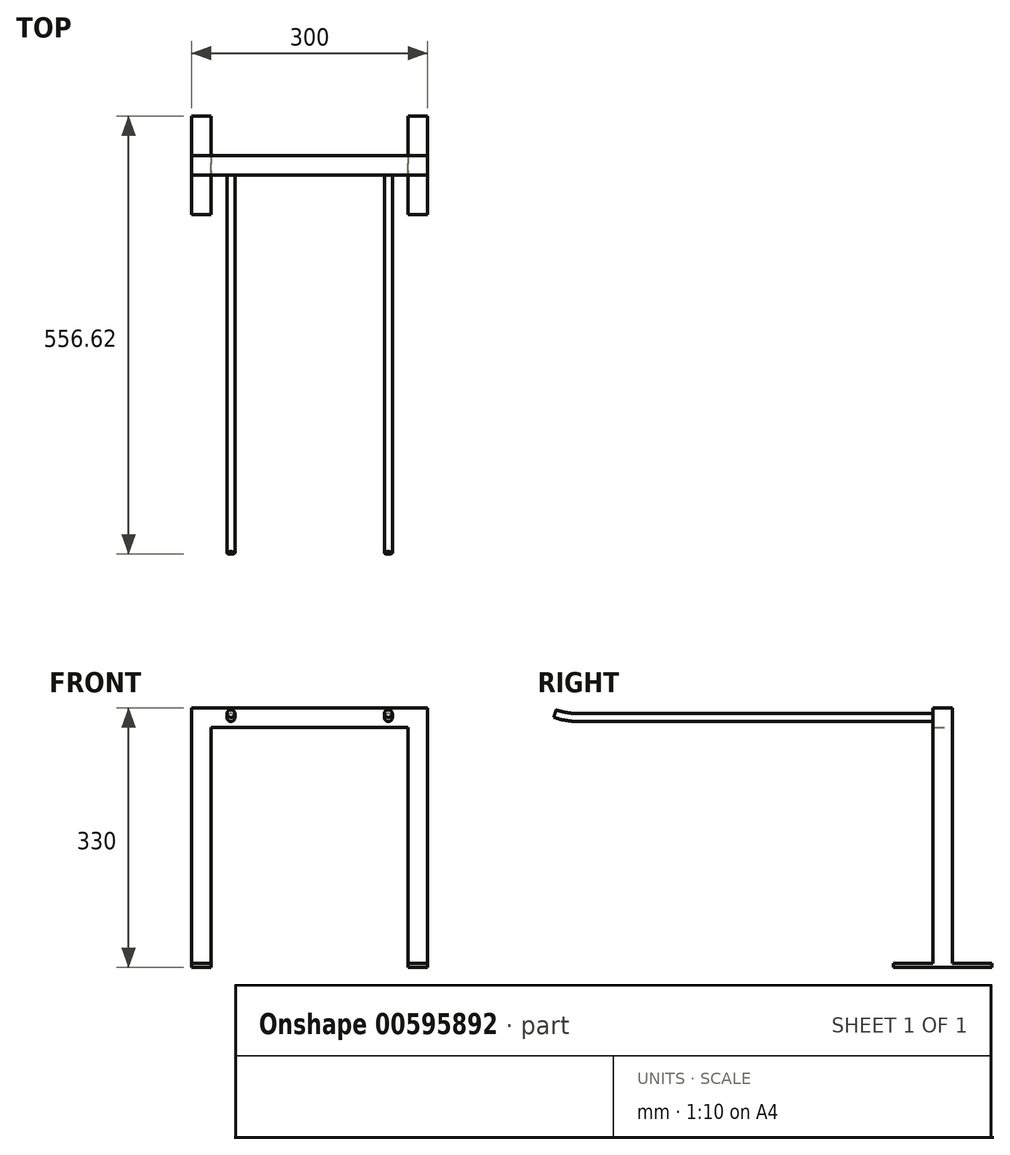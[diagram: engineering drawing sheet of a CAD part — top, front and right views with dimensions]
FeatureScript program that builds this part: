
annotation { "Feature Type Name" : "Feature", "Feature Type Description" : "" }
export const myFeature = defineFeature(function(context is Context, id is Id, definition is map)
    precondition{}
    {
        {
            var Q0;
            Q0=qCreatedBy(makeId("Right.planeOp"),FACE);
            var sketch = newSketch(context, id + "F0", { "sketchPlane" : qUnion([Q0])});
            skLineSegment(sketch, "E0.bottom", {"start": v(12.5, 12.5) * mm, "end": v(-12.5, 12.5) * mm});
            skLineSegment(sketch, "E0.top", {"start": v(12.5, -12.5) * mm, "end": v(-12.5, -12.5) * mm});
            skLineSegment(sketch, "E0.left", {"start": v(12.5, 12.5) * mm, "end": v(12.5, -12.5) * mm});
            skLineSegment(sketch, "E0.right", {"start": v(-12.5, 12.5) * mm, "end": v(-12.5, -12.5) * mm});
            skPoint(sketch, "E0.middle", {"position": v(0, 0) * mm});
            skSolve(sketch);
        }
        {
            var Q0;
            Q0=makeQuery(id+"F0.imprint","IMPRINT",FACE,{"disambiguationData":[TD([[makeQuery(id+"F0.imprint","IMPRINT",EDGE,{"derivedFrom":sQuery(id+"F0.wireOp",EDGE,"E0.bottom")}),1.0]])]});
            extrude(context, id + "F1", {"entities" : qUnion([Q0]), "depth" : 150 * mm, "offsetDistance" : 25.4 * mm, "hasSecondDirection" : true, "secondDirectionOppositeDirection" : true, "secondDirectionDepth" : 150 * mm});
        }
        {
            var Q0;
            Q0=makeQuery(id+"F1.opExtrude","SWEPT_FACE",FACE,{"disambiguationData":[OSD([sQuery(id+"F0.wireOp",EDGE,"E0.right")])]});
            var sketch = newSketch(context, id + "F2", { "sketchPlane" : qUnion([Q0])});
            skLineSegment(sketch, "E1", {"start": v(-150, 0) * mm, "end": v(150, 0) * mm, "construction": true});
            skCircle(sketch, "E2", {"center": v(-100, 0) * mm, "radius": 5 * mm});
            skCircle(sketch, "E3", {"center": v(100, 0) * mm, "radius": 5 * mm});
            skSolve(sketch);
        }
        {
            var Q0;
            Q0=qCreatedBy(makeId("Right.planeOp"),FACE);
            var sketch = newSketch(context, id + "F3", { "sketchPlane" : qUnion([Q0])});
            skLineSegment(sketch, "E4.0", {"start": v(-12.5, -5) * mm, "end": v(-12.5, 5) * mm, "construction": true});
            skLineSegment(sketch, "E5", {"start": v(-12.5, 0) * mm, "end": v(-462.5, 0) * mm});
            skArc(sketch, "E6", {"start": v(-462.5, 0) * mm, "mid": v(-477.7, 1.26) * mm, "end": v(-492.5, 5) * mm});
            skSolve(sketch);
        }
        {
            var Q0;
            Q0 = qSketchRegion(id + "F2", true);
            var Q1;
            Q1 = qConstructionFilter(qBodyType(qCreatedBy(id + "F3" ,EDGE), BodyType.WIRE), ConstructionObject.NO);
            sweep(context, id + "F4", {"operationType" : NewBodyOperationType.ADD, "profiles" : qUnion([Q0]), "path" : qUnion([Q1])});
        }
        {
            var Q0;
            Q0=makeQuery(id+"F1.opExtrude","SWEPT_FACE",FACE,{"disambiguationData":[OSD([sQuery(id+"F0.wireOp",EDGE,"E0.top")])]});
            var sketch = newSketch(context, id + "F5", { "sketchPlane" : qUnion([Q0])});
            skLineSegment(sketch, "E7.bottom", {"start": v(-150, 12.5) * mm, "end": v(-125, 12.5) * mm});
            skLineSegment(sketch, "E7.top", {"start": v(-150, -12.5) * mm, "end": v(-125, -12.5) * mm});
            skLineSegment(sketch, "E7.left", {"start": v(-150, 12.5) * mm, "end": v(-150, -12.5) * mm});
            skLineSegment(sketch, "E7.right", {"start": v(-125, 12.5) * mm, "end": v(-125, -12.5) * mm});
            skLineSegment(sketch, "E8.bottom", {"start": v(150, 12.5) * mm, "end": v(125, 12.5) * mm});
            skLineSegment(sketch, "E8.top", {"start": v(150, -12.5) * mm, "end": v(125, -12.5) * mm});
            skLineSegment(sketch, "E8.left", {"start": v(150, 12.5) * mm, "end": v(150, -12.5) * mm});
            skLineSegment(sketch, "E8.right", {"start": v(125, 12.5) * mm, "end": v(125, -12.5) * mm});
            skSolve(sketch);
        }
        {
            var Q0;
            Q0 = qSketchRegion(id + "F5", true);
            extrude(context, id + "F6", {"entities" : qUnion([Q0]), "operationType" : NewBodyOperationType.ADD, "depth" : 300 * mm, "offsetDistance" : 25 * mm});
        }
        {
            var Q0;
            Q0=makeQuery(id+"F6.opExtrude","CAP_FACE",FACE,{"disambiguationData":[OSD([sQuery(id+"F5.wireOp",EDGE,"E8.bottom"),sQuery(id+"F5.wireOp",EDGE,"E8.top"),sQuery(id+"F5.wireOp",EDGE,"E8.left"),sQuery(id+"F5.wireOp",EDGE,"E8.right")])],"isStart":false});
            var sketch = newSketch(context, id + "F7", { "sketchPlane" : qUnion([Q0])});
            skLineSegment(sketch, "E9.0.0", {"start": v(-125, -12.5) * mm, "end": v(-125, 12.5) * mm});
            skLineSegment(sketch, "E9.0.1", {"start": v(-125, 12.5) * mm, "end": v(-150, 12.5) * mm});
            skLineSegment(sketch, "E9.0.2", {"start": v(-150, 12.5) * mm, "end": v(-150, -12.5) * mm});
            skLineSegment(sketch, "E9.0.3", {"start": v(-150, -12.5) * mm, "end": v(-125, -12.5) * mm});
            skLineSegment(sketch, "E10.bottom", {"start": v(-150, 12.5) * mm, "end": v(-125, 12.5) * mm});
            skLineSegment(sketch, "E10.top", {"start": v(-150, 62.5) * mm, "end": v(-125, 62.5) * mm});
            skLineSegment(sketch, "E10.left", {"start": v(-150, 12.5) * mm, "end": v(-150, 62.5) * mm});
            skLineSegment(sketch, "E10.right", {"start": v(-125, 12.5) * mm, "end": v(-125, 62.5) * mm});
            skLineSegment(sketch, "E11.top", {"start": v(-150, -62.5) * mm, "end": v(-125, -62.5) * mm});
            skLineSegment(sketch, "E11.left", {"start": v(-150, -12.5) * mm, "end": v(-150, -62.5) * mm});
            skLineSegment(sketch, "E11.right", {"start": v(-125, -12.5) * mm, "end": v(-125, -62.5) * mm});
            skLineSegment(sketch, "E12.MirrorCS", {"start": v(150, 12.5) * mm, "end": v(125, 12.5) * mm});
            skLineSegment(sketch, "E13.MirrorCS", {"start": v(150, -12.5) * mm, "end": v(125, -12.5) * mm});
            skLineSegment(sketch, "E14.MirrorCS", {"start": v(125, 12.5) * mm, "end": v(150, 12.5) * mm});
            skLineSegment(sketch, "E15.MirrorCS", {"start": v(125, -12.5) * mm, "end": v(125, 12.5) * mm});
            skLineSegment(sketch, "E16.MirrorCS", {"start": v(150, 12.5) * mm, "end": v(150, -12.5) * mm});
            skLineSegment(sketch, "E17.MirrorCS", {"start": v(150, 62.5) * mm, "end": v(125, 62.5) * mm});
            skLineSegment(sketch, "E18.MirrorCS", {"start": v(150, -62.5) * mm, "end": v(125, -62.5) * mm});
            skLineSegment(sketch, "E19.MirrorCS", {"start": v(125, -12.5) * mm, "end": v(125, -62.5) * mm});
            skLineSegment(sketch, "E20.MirrorCS", {"start": v(150, -12.5) * mm, "end": v(150, -62.5) * mm});
            skLineSegment(sketch, "E21.MirrorCS", {"start": v(150, 12.5) * mm, "end": v(150, 62.5) * mm});
            skLineSegment(sketch, "E22.MirrorCS", {"start": v(125, 12.5) * mm, "end": v(125, 62.5) * mm});
            skSolve(sketch);
        }
        {
            var Q0;
            Q0 = qSketchRegion(id + "F7", true);
            extrude(context, id + "F8", {"entities" : qUnion([Q0]), "operationType" : NewBodyOperationType.ADD, "depth" : 5 * mm, "offsetDistance" : 25 * mm});
        }
    });
